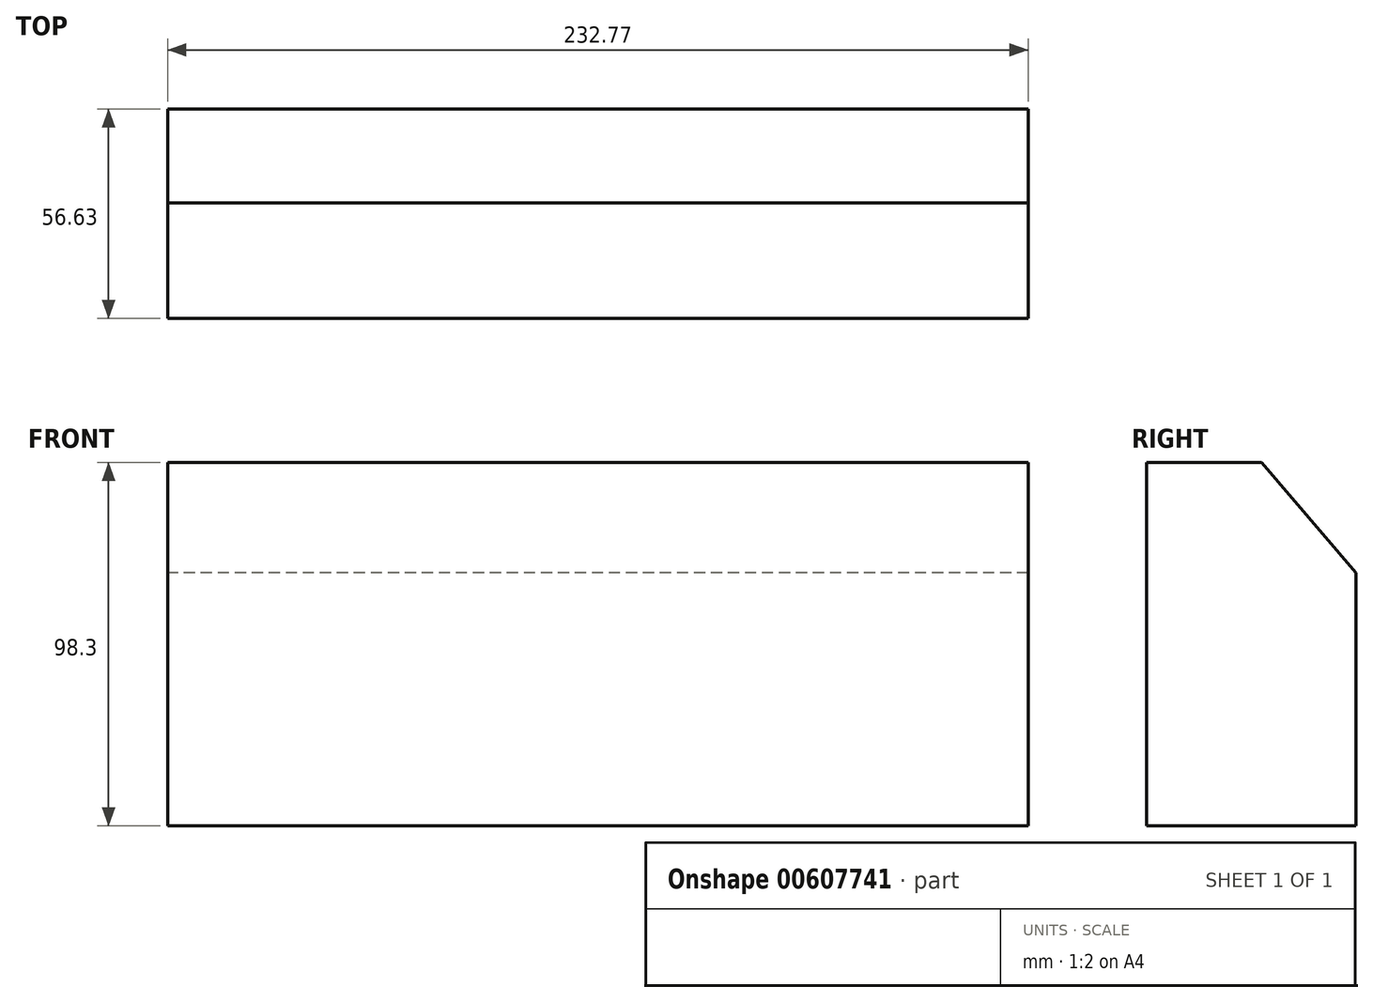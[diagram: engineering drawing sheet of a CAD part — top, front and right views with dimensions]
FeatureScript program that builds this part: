
annotation { "Feature Type Name" : "Feature", "Feature Type Description" : "" }
export const myFeature = defineFeature(function(context is Context, id is Id, definition is map)
    precondition{}
    {
        {
            var Q0;
            Q0=qCreatedBy(makeId("Right.planeOp"),FACE);
            var sketch = newSketch(context, id + "F0", { "sketchPlane" : qUnion([Q0])});
            skLineSegment(sketch, "E0", {"start": v(0, 52.67) * mm, "end": v(31.18, 52.67) * mm});
            skLineSegment(sketch, "E1", {"start": v(31.18, 52.67) * mm, "end": v(56.63, 22.86) * mm});
            skLineSegment(sketch, "E2", {"start": v(56.63, 22.86) * mm, "end": v(56.63, -45.63) * mm});
            skLineSegment(sketch, "E3", {"start": v(56.63, -45.63) * mm, "end": v(0, -45.63) * mm});
            skLineSegment(sketch, "E4", {"start": v(0, -45.63) * mm, "end": v(0, 52.67) * mm});
            skSolve(sketch);
        }
        {
            var Q0;
            Q0=makeQuery(id+"F0.imprint","IMPRINT",FACE,{"disambiguationData":[TD([[makeQuery(id+"F0.imprint","IMPRINT",EDGE,{"derivedFrom":sQuery(id+"F0.wireOp",EDGE,"E0")}),-1.0]])]});
            var sketch = newSketch(context, id + "F1", { "sketchPlane" : qUnion([Q0])});
            skSolve(sketch);
        }
        {
            var Q0;
            Q0=makeQuery(id+"F0.imprint","IMPRINT",FACE,{"disambiguationData":[TD([[makeQuery(id+"F0.imprint","IMPRINT",EDGE,{"derivedFrom":sQuery(id+"F0.wireOp",EDGE,"E0")}),-1.0]])]});
            var Q1;
            Q1 = qSketchRegion(id + "F1", true);
            extrude(context, id + "F2", {"entities" : qUnion([Q0, Q1]), "depth" : 232.77 * mm, "offsetDistance" : 25.4 * mm});
        }
    });
